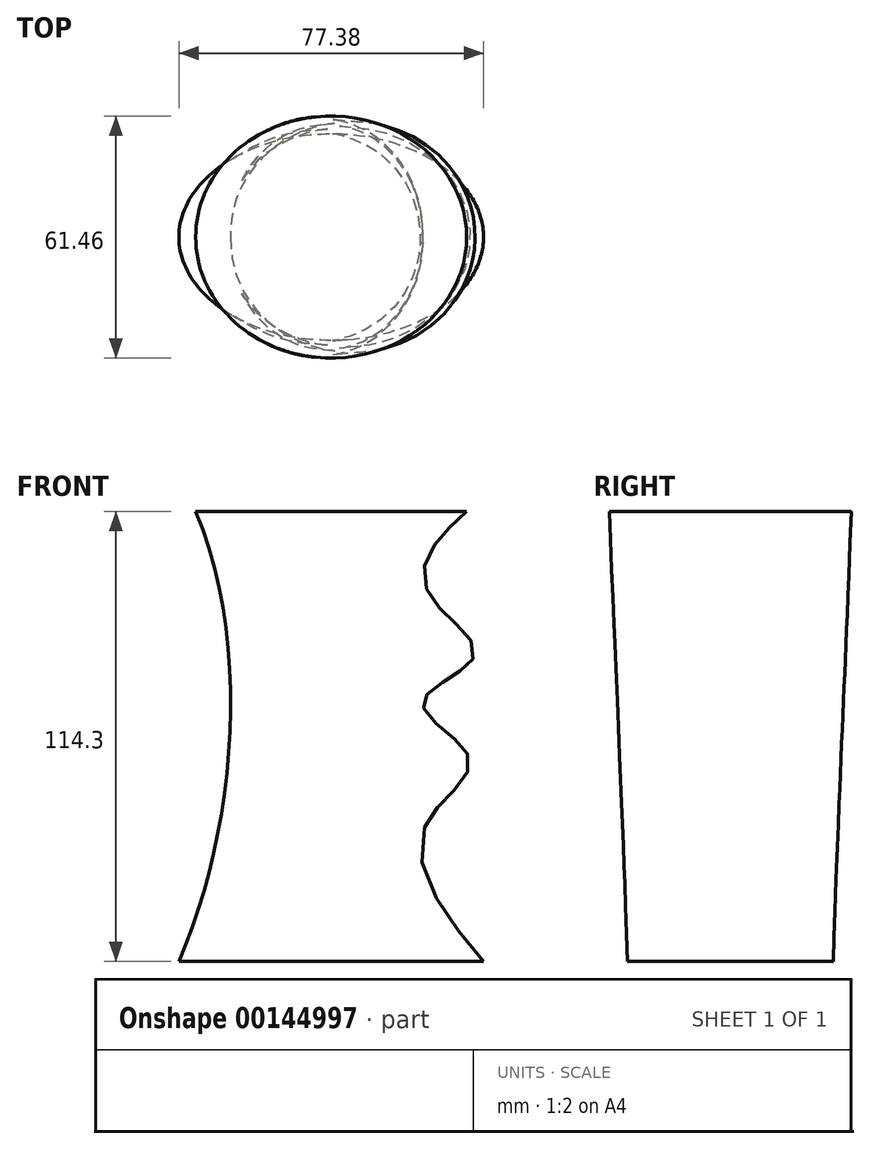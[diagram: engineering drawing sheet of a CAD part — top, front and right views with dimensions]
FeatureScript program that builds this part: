
annotation { "Feature Type Name" : "Feature", "Feature Type Description" : "" }
export const myFeature = defineFeature(function(context is Context, id is Id, definition is map)
    precondition{}
    {
        {
            var Q0;
            Q0=qCreatedBy(makeId("Front.planeOp"),FACE);
            var sketch = newSketch(context, id + "F0", { "sketchPlane" : qUnion([Q0])});
            skLineSegment(sketch, "E0", {"start": v(0, 0) * mm, "end": v(0, 127) * mm});
            skSolve(sketch);
        }
        {
            var Q0;
            Q0=qCreatedBy(makeId("Top.planeOp"),FACE);
            cPlane(context, id + "F1", {"entities" : qUnion([Q0]), "cplaneType" : CPlaneType.OFFSET, "offset" : 12.7 * mm, "width" : 152.4 * mm, "height" : 152.4 * mm});
        }
        {
            var Q0;
            Q0=qCreatedBy(id+"F1.planeOp",FACE);
            var Q1;
            Q1=sQuery(id+"F0.wireOp",VERTEX,"E0.end");
            cPlane(context, id + "F2", {"entities" : qUnion([Q0, Q1]), "cplaneType" : CPlaneType.PLANE_POINT, "offset" : 152.4 * mm, "width" : 152.4 * mm, "height" : 152.4 * mm});
        }
        {
            var Q0;
            Q0=qCreatedBy(id+"F1.planeOp",FACE);
            var sketch = newSketch(context, id + "F3", { "sketchPlane" : qUnion([Q0])});
            skEllipse(sketch, "E1", {"center": v(0, 0) * mm, "majorRadius": 38.7 * mm, "minorRadius": 26.14 * mm, "majorAxis": v(1, 0)});
            skSolve(sketch);
        }
        {
            var Q0;
            Q0=qCreatedBy(id+"F2.planeOp",FACE);
            var sketch = newSketch(context, id + "F4", { "sketchPlane" : qUnion([Q0])});
            skEllipse(sketch, "E2", {"center": v(0, 0) * mm, "majorRadius": 34.41 * mm, "minorRadius": 30.73 * mm, "majorAxis": v(1, 0)});
            skSolve(sketch);
        }
        {
            var Q0;
            Q0=qCreatedBy(makeId("Front.planeOp"),FACE);
            var sketch = newSketch(context, id + "F5", { "sketchPlane" : qUnion([Q0])});
            skFitSpline(sketch, "E3", {"points": [v(-34.41, 127) * mm, v(-38.7, 12.7) * mm], "startDerivative": vector(44.25, -105.67) * mm, "endDerivative": vector(-41.24, -94.6) * mm});
            skSolve(sketch);
        }
        {
            var Q0;
            Q0=qCreatedBy(makeId("Front.planeOp"),FACE);
            var sketch = newSketch(context, id + "F6", { "sketchPlane" : qUnion([Q0])});
            skFitSpline(sketch, "E4", {"points": [v(34.41, 127) * mm, v(24.56, 106.54) * mm, v(36.43, 90.52) * mm, v(23.3, 78.37) * mm, v(35.17, 64.1) * mm, v(23.55, 46.42) * mm, v(38.7, 12.7) * mm], "startDerivative": vector(-154.43, -133.87) * mm, "endDerivative": vector(146.55, -167.72) * mm});
            skSolve(sketch);
        }
        {
            var Q0;
            Q0=makeQuery(id+"F4.imprint","IMPRINT",FACE,{"disambiguationData":[TD([[makeQuery(id+"F4.imprint","IMPRINT",EDGE,{"derivedFrom":sQuery(id+"F4.wireOp",EDGE,"E2")}),1.0]])]});
            var Q1;
            Q1=makeQuery(id+"F3.imprint","IMPRINT",FACE,{"disambiguationData":[TD([[makeQuery(id+"F3.imprint","IMPRINT",EDGE,{"derivedFrom":sQuery(id+"F3.wireOp",EDGE,"E1")}),1.0]])]});
            var Q2;
            Q2=sQuery(id+"F5.wireOp",EDGE,"E3");
            var Q3;
            Q3=sQuery(id+"F6.wireOp",EDGE,"E4");
            loft(context, id + "F7", {"addGuides" : true, "sheetProfilesArray" : [{ "sheetProfileEntities" : qUnion([Q0]) }, { "sheetProfileEntities" : qUnion([Q1]) }], "guidesArray" : [{ "guideEntities" : qUnion([Q2]), "guideDerivativeType" : LoftGuideDerivativeType.DEFAULT, "guideDerivativeMagnitude" : 1 }, { "guideEntities" : qUnion([Q3]), "guideDerivativeType" : LoftGuideDerivativeType.DEFAULT, "guideDerivativeMagnitude" : 1 }]});
        }
    });
